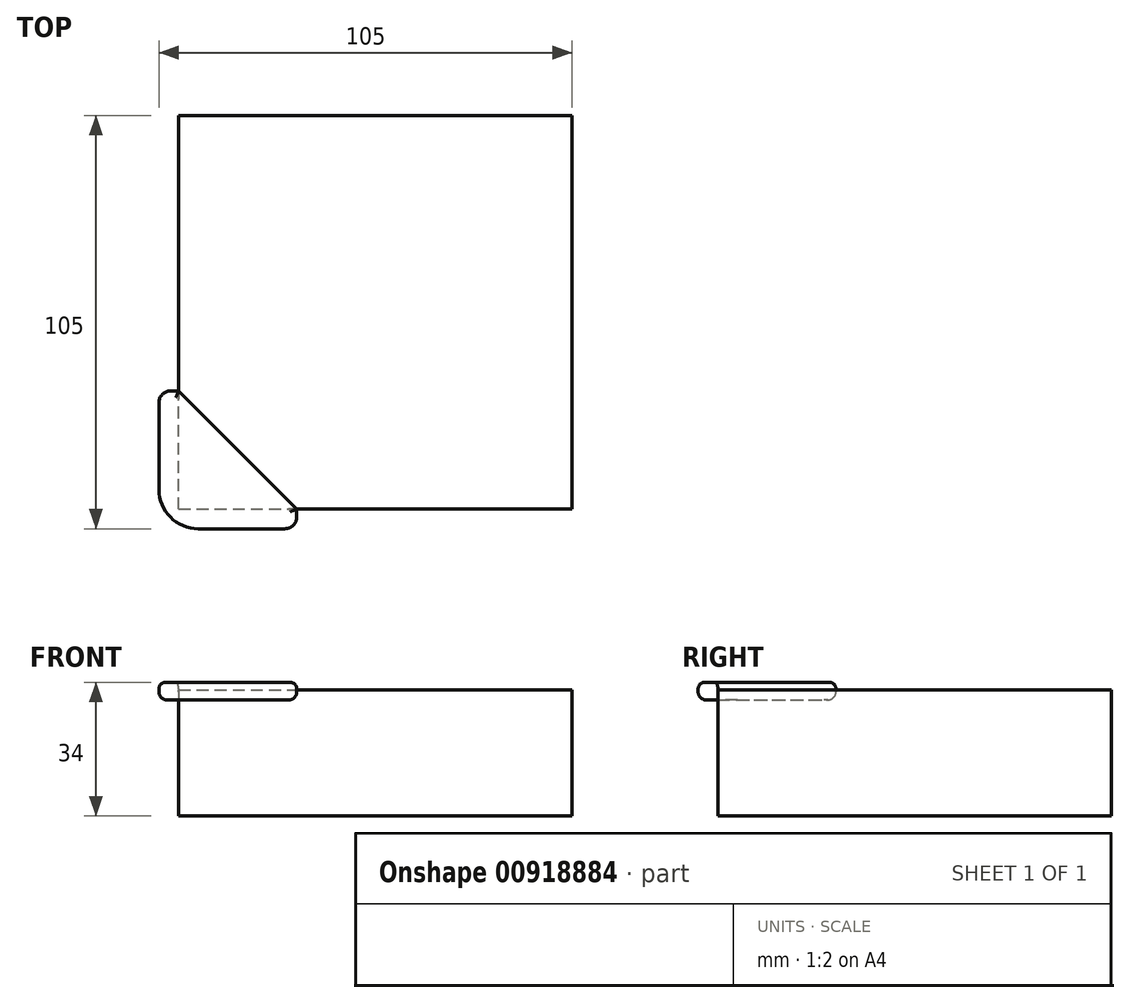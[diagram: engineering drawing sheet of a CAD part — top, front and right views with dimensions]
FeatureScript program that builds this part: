
annotation { "Feature Type Name" : "Feature", "Feature Type Description" : "" }
export const myFeature = defineFeature(function(context is Context, id is Id, definition is map)
    precondition{}
    {
        {
            var Q0;
            Q0=qCreatedBy(makeId("Top.planeOp"),FACE);
            var sketch = newSketch(context, id + "F0", { "sketchPlane" : qUnion([Q0])});
            skLineSegment(sketch, "E0.bottom", {"start": v(0, 0) * mm, "end": v(100, 0) * mm});
            skLineSegment(sketch, "E0.top", {"start": v(0, 100) * mm, "end": v(100, 100) * mm});
            skLineSegment(sketch, "E0.left", {"start": v(0, 0) * mm, "end": v(0, 100) * mm});
            skLineSegment(sketch, "E0.right", {"start": v(100, 0) * mm, "end": v(100, 100) * mm});
            skSolve(sketch);
        }
        {
            var Q0;
            Q0 = qSketchRegion(id + "F0", true);
            var Q1;
            Q1=makeQuery(id+"F0.imprint","IMPRINT",FACE,{"disambiguationData":[TD([[makeQuery(id+"F0.imprint","IMPRINT",EDGE,{"derivedFrom":sQuery(id+"F0.wireOp",EDGE,"E0.bottom")}),1.0]])]});
            extrude(context, id + "F1", {"entities" : qUnion([Q0, Q1]), "depth" : 32 * mm, "offsetDistance" : 25 * mm});
        }
        {
            var Q0;
            Q0=makeQuery(id+"F1.opExtrude","CAP_FACE",FACE,{"disambiguationData":[OSD([sQuery(id+"F0.wireOp",EDGE,"E0.bottom"),sQuery(id+"F0.wireOp",EDGE,"E0.top"),sQuery(id+"F0.wireOp",EDGE,"E0.left"),sQuery(id+"F0.wireOp",EDGE,"E0.right")])],"isStart":false});
            var sketch = newSketch(context, id + "F2", { "sketchPlane" : qUnion([Q0])});
            skLineSegment(sketch, "E1", {"start": v(0, 0) * mm, "end": v(30, 0) * mm});
            skLineSegment(sketch, "E2", {"start": v(0, 0) * mm, "end": v(0, 30) * mm});
            skLineSegment(sketch, "E3", {"start": v(0, 30) * mm, "end": v(30, 0) * mm});
            skLineSegment(sketch, "E4.0", {"start": v(-5, 5) * mm, "end": v(-5, 27) * mm});
            skLineSegment(sketch, "E5.0", {"start": v(5, -5) * mm, "end": v(27.02, -5) * mm});
            skPoint(sketch, "E6", {"position": v(-5, -5) * mm});
            skPoint(sketch, "E7.orphan", {"position": v(-5, 0) * mm});
            skPoint(sketch, "E8.orphan", {"position": v(0, -5) * mm});
            skLineSegment(sketch, "E9", {"start": v(30, 0) * mm, "end": v(30.02, -1.98) * mm});
            skLineSegment(sketch, "E10", {"start": v(-2, 30) * mm, "end": v(0, 30) * mm});
            skArc(sketch, "E11.filletArc", {"start": v(-5, 5) * mm, "mid": v(-2.07, -2.07) * mm, "end": v(5, -5) * mm});
            skPoint(sketch, "E12.visualSharp", {"position": v(-5, 30) * mm});
            skArc(sketch, "E12.filletArc", {"start": v(-2, 30) * mm, "mid": v(-4.12, 29.12) * mm, "end": v(-5, 27) * mm});
            skPoint(sketch, "E13.visualSharp", {"position": v(30.04, -5) * mm});
            skArc(sketch, "E13.filletArc", {"start": v(27.02, -5) * mm, "mid": v(29.15, -4.11) * mm, "end": v(30.02, -1.98) * mm});
            skSolve(sketch);
        }
        {
            var Q0;
            Q0=makeQuery(id+"F2.imprint","IMPRINT",FACE,{"disambiguationData":[TD([[makeQuery(id+"F2.imprint","IMPRINT",EDGE,{"derivedFrom":sQuery(id+"F2.wireOp",EDGE,"E1")}),1.0]])]});
            var Q1;
            Q1=makeQuery(id+"F2.imprint","IMPRINT",FACE,{"disambiguationData":[TD([[makeQuery(id+"F2.imprint","IMPRINT",EDGE,{"derivedFrom":sQuery(id+"F2.wireOp",EDGE,"E1")}),-1.0]])]});
            extrude(context, id + "F3", {"entities" : qUnion([Q0, Q1]), "surfaceOperationType" : NewSurfaceOperationType.ADD, "depth" : 2 * mm, "offsetDistance" : 25 * mm});
        }
        {
            var Q0;
            Q0=makeQuery(id+"F2.imprint","IMPRINT",FACE,{"disambiguationData":[TD([[makeQuery(id+"F2.imprint","IMPRINT",EDGE,{"derivedFrom":sQuery(id+"F2.wireOp",EDGE,"E1")}),-1.0]])]});
            extrude(context, id + "F4", {"entities" : qUnion([Q0]), "operationType" : NewBodyOperationType.ADD, "oppositeDirection" : true, "depth" : 2.5 * mm, "offsetDistance" : 25 * mm});
        }
        {
            var Q0;
            Q0=makeQuery(id+"F4.opExtrude","CAP_EDGE",EDGE,{"disambiguationData":[OSD([sQuery(id+"F2.wireOp",EDGE,"E10")])],"isStart":false});
            var Q1;
            Q1=makeQuery(id+"F4.opExtrude","CAP_EDGE",EDGE,{"disambiguationData":[OSD([sQuery(id+"F2.wireOp",EDGE,"E12.filletArc")])],"isStart":false});
            var Q2;
            Q2=makeQuery(id+"F4.opExtrude","CAP_EDGE",EDGE,{"disambiguationData":[OSD([sQuery(id+"F2.wireOp",EDGE,"E4.0")])],"isStart":false});
            var Q3;
            Q3=makeQuery(id+"F4.opExtrude","CAP_EDGE",EDGE,{"disambiguationData":[OSD([sQuery(id+"F2.wireOp",EDGE,"E11.filletArc")])],"isStart":false});
            var Q4;
            Q4=makeQuery(id+"F4.opExtrude","CAP_EDGE",EDGE,{"disambiguationData":[OSD([sQuery(id+"F2.wireOp",EDGE,"E5.0")])],"isStart":false});
            var Q5;
            Q5=makeQuery(id+"F4.opExtrude","CAP_EDGE",EDGE,{"disambiguationData":[OSD([sQuery(id+"F2.wireOp",EDGE,"E13.filletArc")])],"isStart":false});
            var Q6;
            Q6=makeQuery(id+"F4.opExtrude","CAP_EDGE",EDGE,{"disambiguationData":[OSD([sQuery(id+"F2.wireOp",EDGE,"E9")])],"isStart":false});
            fillet(context, id + "F5", {"entities" : qUnion([Q0, Q1, Q2, Q3, Q4, Q5, Q6]), "radius" : 2 * mm, "tangentPropagation" : true, "allowEdgeOverflow" : false});
        }
        {
            var Q0;
            Q0=makeQuery(id+"F3.opExtrude","CAP_FACE",FACE,{"disambiguationData":[OSD([sQuery(id+"F2.wireOp",EDGE,"E3"),sQuery(id+"F2.wireOp",EDGE,"E4.0"),sQuery(id+"F2.wireOp",EDGE,"E5.0"),sQuery(id+"F2.wireOp",EDGE,"E9"),sQuery(id+"F2.wireOp",EDGE,"E10"),sQuery(id+"F2.wireOp",EDGE,"E11.filletArc"),sQuery(id+"F2.wireOp",EDGE,"E12.filletArc"),sQuery(id+"F2.wireOp",EDGE,"E13.filletArc")])],"isStart":false});
            fillet(context, id + "F6", {"entities" : qUnion([Q0]), "radius" : 1.69 * mm, "tangentPropagation" : true, "allowEdgeOverflow" : false});
        }
    });
